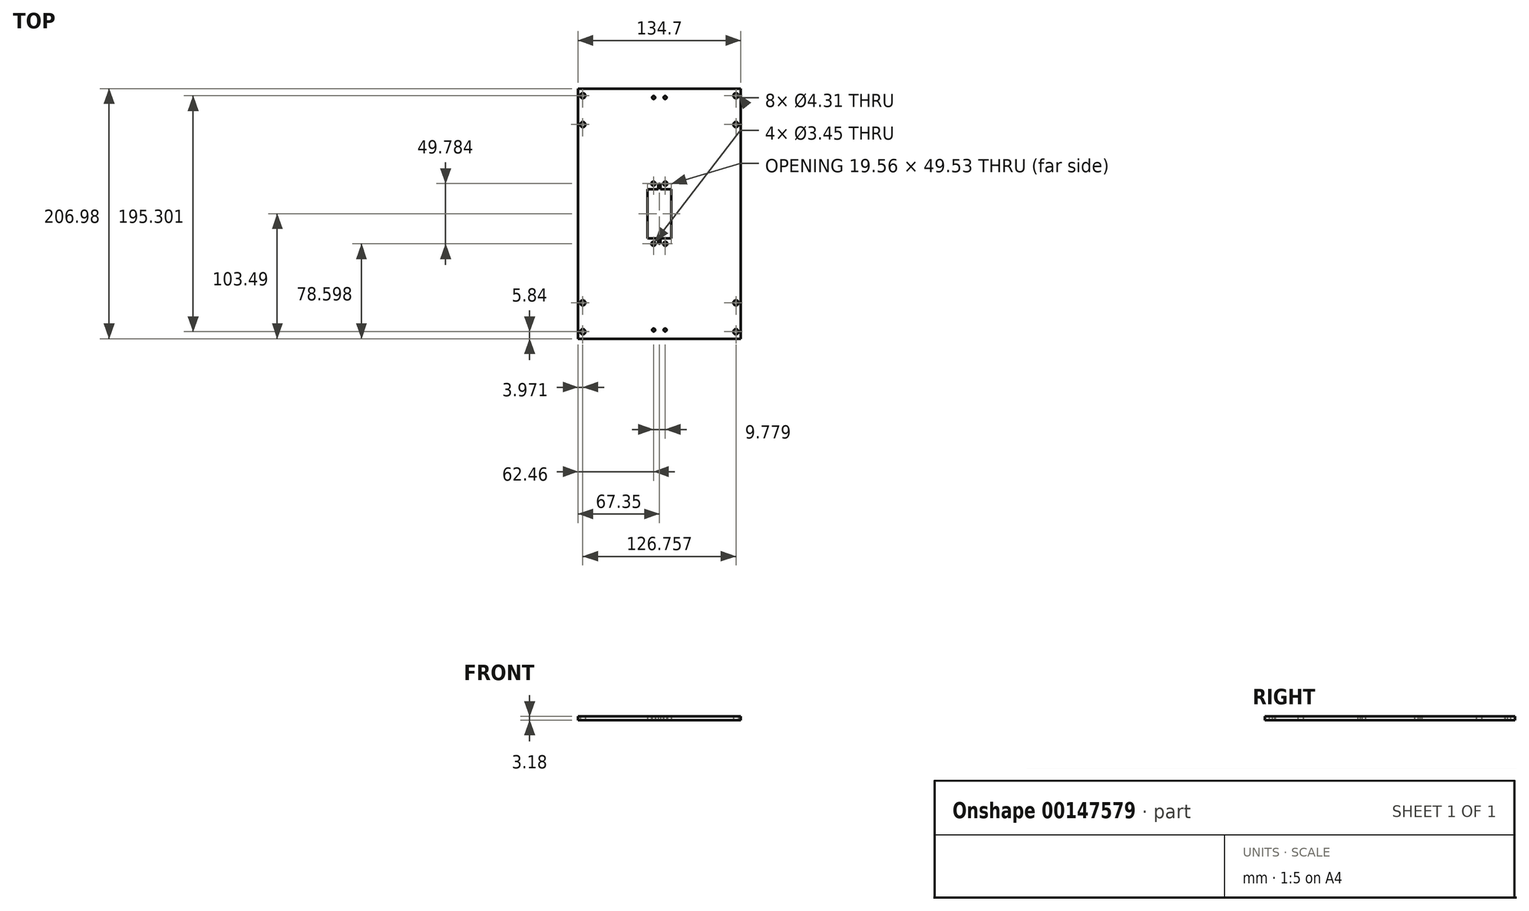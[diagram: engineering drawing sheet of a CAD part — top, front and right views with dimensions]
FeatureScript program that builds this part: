
annotation { "Feature Type Name" : "Feature", "Feature Type Description" : "" }
export const myFeature = defineFeature(function(context is Context, id is Id, definition is map)
    precondition{}
    {
        {
            var Q0;
            Q0=qCreatedBy(makeId("Top.planeOp"),FACE);
            var sketch = newSketch(context, id + "F0", { "sketchPlane" : qUnion([Q0])});
            skLineSegment(sketch, "E0.rect.bottom", {"start": v(-9.78, -20.32) * mm, "end": v(-9.78, 20.32) * mm});
            skLineSegment(sketch, "E0.rect.top", {"start": v(9.78, -20.32) * mm, "end": v(9.78, 20.32) * mm});
            skPoint(sketch, "E0.rect.middle", {"position": v(0, 0) * mm});
            skLineSegment(sketch, "E1.rect.bottom", {"start": v(-4.89, -24.9) * mm, "end": v(-4.89, 24.9) * mm, "construction": true});
            skLineSegment(sketch, "E1.rect.top", {"start": v(4.89, -24.9) * mm, "end": v(4.89, 24.9) * mm, "construction": true});
            skLineSegment(sketch, "E1.rect.left", {"start": v(-4.89, -24.9) * mm, "end": v(4.89, -24.9) * mm, "construction": true});
            skLineSegment(sketch, "E1.rect.right", {"start": v(-4.89, 24.9) * mm, "end": v(4.89, 24.9) * mm, "construction": true});
            skCircle(sketch, "E2", {"center": v(4.89, 24.9) * mm, "radius": 1.73 * mm});
            skCircle(sketch, "E3", {"center": v(-4.89, 24.9) * mm, "radius": 1.73 * mm});
            skCircle(sketch, "E4", {"center": v(4.89, -24.9) * mm, "radius": 1.73 * mm});
            skCircle(sketch, "E5", {"center": v(-4.89, -24.9) * mm, "radius": 1.73 * mm});
            skLineSegment(sketch, "E6", {"start": v(-9.78, 20.32) * mm, "end": v(-1.02, 20.32) * mm});
            skLineSegment(sketch, "E7", {"start": v(-1.02, 20.32) * mm, "end": v(-1.02, 23.75) * mm});
            skLineSegment(sketch, "E8", {"start": v(-1.02, 23.75) * mm, "end": v(1.02, 23.75) * mm, "construction": true});
            skLineSegment(sketch, "E9", {"start": v(1.02, 23.75) * mm, "end": v(1.02, 20.32) * mm});
            skLineSegment(sketch, "E10", {"start": v(1.02, 20.32) * mm, "end": v(9.78, 20.32) * mm});
            skLineSegment(sketch, "E11", {"start": v(9.78, -20.32) * mm, "end": v(1.02, -20.32) * mm});
            skLineSegment(sketch, "E12", {"start": v(1.02, -20.32) * mm, "end": v(1.02, -23.75) * mm});
            skLineSegment(sketch, "E13", {"start": v(1.02, -23.75) * mm, "end": v(-1.02, -23.75) * mm, "construction": true});
            skLineSegment(sketch, "E14", {"start": v(-1.02, -23.75) * mm, "end": v(-1.02, -20.32) * mm});
            skLineSegment(sketch, "E15", {"start": v(-1.02, -20.32) * mm, "end": v(-9.78, -20.32) * mm});
            skArc(sketch, "E16", {"start": v(1.02, 23.75) * mm, "mid": v(0, 24.77) * mm, "end": v(-1.02, 23.75) * mm});
            skArc(sketch, "E17", {"start": v(-1.02, -23.75) * mm, "mid": v(0, -24.76) * mm, "end": v(1.02, -23.75) * mm});
            skLineSegment(sketch, "E18", {"start": v(-1.02, 20.32) * mm, "end": v(1.02, 20.32) * mm, "construction": true});
            skLineSegment(sketch, "E19", {"start": v(0, 20.32) * mm, "end": v(0, 10.9) * mm, "construction": true});
            skLineSegment(sketch, "E20.bottom", {"start": v(67.35, -103.5) * mm, "end": v(-67.35, -103.5) * mm});
            skLineSegment(sketch, "E20.top", {"start": v(67.35, 103.5) * mm, "end": v(-67.35, 103.5) * mm});
            skLineSegment(sketch, "E20.left", {"start": v(67.35, -103.5) * mm, "end": v(67.35, 103.5) * mm});
            skLineSegment(sketch, "E20.right", {"start": v(-67.35, -103.5) * mm, "end": v(-67.35, 103.5) * mm});
            skLineSegment(sketch, "E21", {"start": v(0, 0) * mm, "end": v(0, 0) * mm});
            skLineSegment(sketch, "E22.bottom", {"start": v(-63.38, 73.77) * mm, "end": v(63.38, 73.77) * mm, "construction": true});
            skLineSegment(sketch, "E22.top", {"start": v(-63.38, -73.77) * mm, "end": v(63.38, -73.77) * mm, "construction": true});
            skLineSegment(sketch, "E22.left", {"start": v(-63.38, 73.77) * mm, "end": v(-63.38, -73.77) * mm, "construction": true});
            skLineSegment(sketch, "E22.right", {"start": v(63.38, 73.77) * mm, "end": v(63.38, -73.77) * mm, "construction": true});
            skCircle(sketch, "E23", {"center": v(-63.38, 73.77) * mm, "radius": 2.15 * mm});
            skCircle(sketch, "E24", {"center": v(63.38, 73.77) * mm, "radius": 2.15 * mm});
            skCircle(sketch, "E25", {"center": v(-63.38, -73.77) * mm, "radius": 2.15 * mm});
            skCircle(sketch, "E26", {"center": v(63.38, -73.77) * mm, "radius": 2.15 * mm});
            skLineSegment(sketch, "E27", {"start": v(63.38, 73.77) * mm, "end": v(63.38, 97.65) * mm, "construction": true});
            skLineSegment(sketch, "E28", {"start": v(-63.38, 73.77) * mm, "end": v(-63.38, 97.65) * mm, "construction": true});
            skLineSegment(sketch, "E29", {"start": v(-63.38, -73.77) * mm, "end": v(-63.38, -97.65) * mm, "construction": true});
            skLineSegment(sketch, "E30", {"start": v(63.38, -73.77) * mm, "end": v(63.38, -97.65) * mm, "construction": true});
            skCircle(sketch, "E31", {"center": v(-63.38, 97.65) * mm, "radius": 2.15 * mm});
            skCircle(sketch, "E32", {"center": v(63.38, 97.65) * mm, "radius": 2.15 * mm});
            skCircle(sketch, "E33", {"center": v(63.38, -97.65) * mm, "radius": 2.15 * mm});
            skCircle(sketch, "E34", {"center": v(-63.38, -97.65) * mm, "radius": 2.15 * mm});
            skLineSegment(sketch, "E35", {"start": v(63.38, 97.65) * mm, "end": v(63.38, 103.5) * mm, "construction": true});
            skLineSegment(sketch, "E36", {"start": v(63.38, 97.65) * mm, "end": v(67.35, 97.65) * mm, "construction": true});
            skLineSegment(sketch, "E37", {"start": v(-63.38, -97.65) * mm, "end": v(-63.38, -103.5) * mm, "construction": true});
            skLineSegment(sketch, "E38", {"start": v(-63.38, -97.65) * mm, "end": v(-67.35, -97.65) * mm, "construction": true});
            skLineSegment(sketch, "E39", {"start": v(0, -103.5) * mm, "end": v(0, -96.2) * mm, "construction": true});
            skLineSegment(sketch, "E40", {"start": v(-4.75, -96.2) * mm, "end": v(4.75, -96.2) * mm, "construction": true});
            skLineSegment(sketch, "E41", {"start": v(0, 103.5) * mm, "end": v(0, 96.2) * mm, "construction": true});
            skLineSegment(sketch, "E42", {"start": v(-4.75, 96.2) * mm, "end": v(4.75, 96.2) * mm, "construction": true});
            skCircle(sketch, "E43", {"center": v(-4.75, -96.2) * mm, "radius": 1.25 * mm});
            skCircle(sketch, "E44", {"center": v(4.75, -96.2) * mm, "radius": 1.25 * mm});
            skCircle(sketch, "E45", {"center": v(-4.75, 96.2) * mm, "radius": 1.25 * mm});
            skCircle(sketch, "E46", {"center": v(4.75, 96.2) * mm, "radius": 1.25 * mm});
            skSolve(sketch);
        }
        {
            var Q0;
            Q0=qSketchRegion(id+"F0",true);
            extrude(context, id + "F1", {"entities" : qUnion([Q0]), "depth" : 3.17 * mm});
        }
    });
